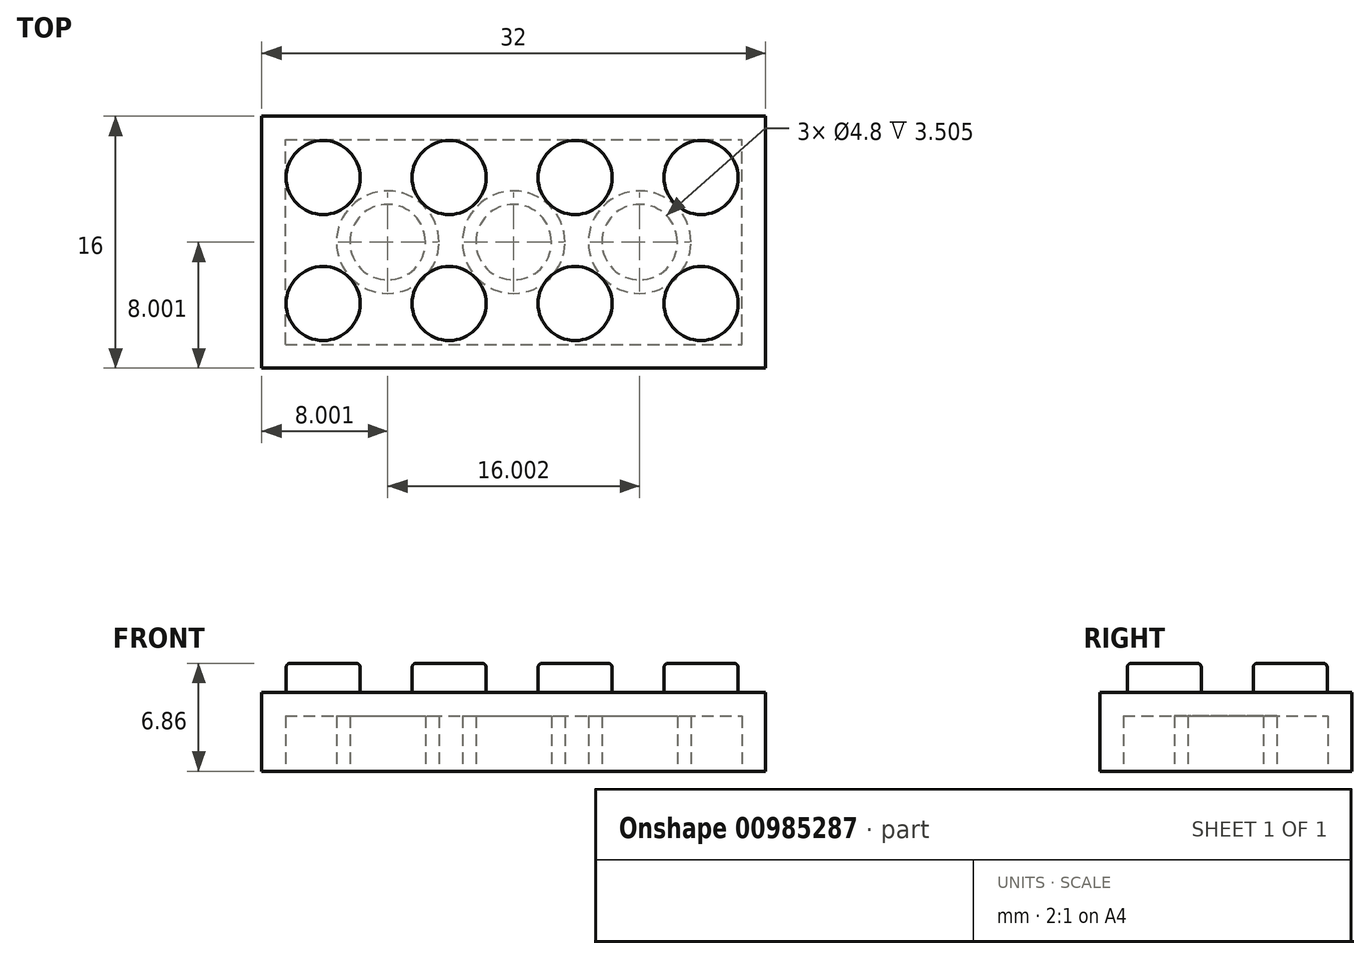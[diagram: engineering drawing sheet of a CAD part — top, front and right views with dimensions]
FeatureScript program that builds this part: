
annotation { "Feature Type Name" : "Feature", "Feature Type Description" : "" }
export const myFeature = defineFeature(function(context is Context, id is Id, definition is map)
    precondition{}
    {
        {
            var Q0;
            Q0=qCreatedBy(makeId("Top.planeOp"),FACE);
            var sketch = newSketch(context, id + "F0", { "sketchPlane" : qUnion([Q0])});
            skLineSegment(sketch, "E0.bottom", {"start": v(0, 0) * mm, "end": v(32, 0) * mm});
            skLineSegment(sketch, "E0.top", {"start": v(0, 16) * mm, "end": v(32, 16) * mm});
            skLineSegment(sketch, "E0.left", {"start": v(0, 0) * mm, "end": v(0, 16) * mm});
            skLineSegment(sketch, "E0.right", {"start": v(32, 0) * mm, "end": v(32, 16) * mm});
            skSolve(sketch);
        }
        {
            var Q0;
            Q0=makeQuery(id+"F0.imprint","IMPRINT",FACE,{"disambiguationData":[TD([[makeQuery(id+"F0.imprint","IMPRINT",EDGE,{"derivedFrom":sQuery(id+"F0.wireOp",EDGE,"E0.bottom")}),1.0]])]});
            extrude(context, id + "F1", {"entities" : qUnion([Q0]), "depth" : 5 * mm, "offsetDistance" : 25.4 * mm});
        }
        {
            var Q0;
            Q0=makeQuery(id+"F1.opExtrude","CAP_FACE",FACE,{"disambiguationData":[OSD([sQuery(id+"F0.wireOp",EDGE,"E0.bottom"),sQuery(id+"F0.wireOp",EDGE,"E0.top"),sQuery(id+"F0.wireOp",EDGE,"E0.left"),sQuery(id+"F0.wireOp",EDGE,"E0.right")])],"isStart":false});
            var sketch = newSketch(context, id + "F2", { "sketchPlane" : qUnion([Q0])});
            skCircle(sketch, "E1", {"center": v(3.9, 12.1) * mm, "radius": 2.35 * mm});
            skCircle(sketch, "E2.0.1.0", {"center": v(3.9, 4.1) * mm, "radius": 2.35 * mm});
            skCircle(sketch, "E2.1.0.0", {"center": v(11.9, 12.1) * mm, "radius": 2.35 * mm});
            skCircle(sketch, "E2.1.1.0", {"center": v(11.9, 4.1) * mm, "radius": 2.35 * mm});
            skCircle(sketch, "E2.2.0.0", {"center": v(19.9, 12.1) * mm, "radius": 2.35 * mm});
            skCircle(sketch, "E2.2.1.0", {"center": v(19.9, 4.1) * mm, "radius": 2.35 * mm});
            skCircle(sketch, "E2.3.0.0", {"center": v(27.9, 12.1) * mm, "radius": 2.35 * mm});
            skCircle(sketch, "E2.3.1.0", {"center": v(27.9, 4.1) * mm, "radius": 2.35 * mm});
            skLineSegment(sketch, "E2.direction1", {"start": v(3.9, 12.1) * mm, "end": v(11.9, 12.1) * mm, "construction": true});
            skLineSegment(sketch, "E2.direction2", {"start": v(3.9, 12.1) * mm, "end": v(3.9, 4.1) * mm, "construction": true});
            skSolve(sketch);
        }
        {
            var Q0;
            Q0 = qSketchRegion(id + "F2", true);
            extrude(context, id + "F3", {"entities" : qUnion([Q0]), "operationType" : NewBodyOperationType.ADD, "depth" : 1.85 * mm, "offsetDistance" : 25.4 * mm});
        }
        {
            var Q0;
            Q0=makeQuery(id+"F3.opExtrude","CAP_EDGE",EDGE,{"disambiguationData":[OSD([sQuery(id+"F2.wireOp",EDGE,"E1")])],"isStart":false});
            var Q1;
            Q1=makeQuery(id+"F3.opExtrude","CAP_FACE",FACE,{"disambiguationData":[OSD([sQuery(id+"F2.wireOp",EDGE,"E2.1.0.0")])],"isStart":false});
            var Q2;
            Q2=makeQuery(id+"F3.opExtrude","CAP_FACE",FACE,{"disambiguationData":[OSD([sQuery(id+"F2.wireOp",EDGE,"E2.2.0.0")])],"isStart":false});
            var Q3;
            Q3=makeQuery(id+"F3.opExtrude","CAP_FACE",FACE,{"disambiguationData":[OSD([sQuery(id+"F2.wireOp",EDGE,"E2.3.0.0")])],"isStart":false});
            var Q4;
            Q4=makeQuery(id+"F3.opExtrude","CAP_FACE",FACE,{"disambiguationData":[OSD([sQuery(id+"F2.wireOp",EDGE,"E2.3.1.0")])],"isStart":false});
            var Q5;
            Q5=makeQuery(id+"F3.opExtrude","CAP_FACE",FACE,{"disambiguationData":[OSD([sQuery(id+"F2.wireOp",EDGE,"E2.2.1.0")])],"isStart":false});
            var Q6;
            Q6=makeQuery(id+"F3.opExtrude","CAP_FACE",FACE,{"disambiguationData":[OSD([sQuery(id+"F2.wireOp",EDGE,"E2.1.1.0")])],"isStart":false});
            var Q7;
            Q7=makeQuery(id+"F3.opExtrude","CAP_FACE",FACE,{"disambiguationData":[OSD([sQuery(id+"F2.wireOp",EDGE,"E2.0.1.0")])],"isStart":false});
            fillet(context, id + "F4", {"entities" : qUnion([Q0, Q1, Q2, Q3, Q4, Q5, Q6, Q7]), "radius" : 0.25 * mm, "tangentPropagation" : true, "allowEdgeOverflow" : false});
        }
        {
            var Q0;
            Q0=makeQuery(id+"F1.opExtrude","CAP_FACE",FACE,{"disambiguationData":[OSD([sQuery(id+"F0.wireOp",EDGE,"E0.bottom"),sQuery(id+"F0.wireOp",EDGE,"E0.top"),sQuery(id+"F0.wireOp",EDGE,"E0.left"),sQuery(id+"F0.wireOp",EDGE,"E0.right")])],"isStart":true});
            var sketch = newSketch(context, id + "F5", { "sketchPlane" : qUnion([Q0])});
            skLineSegment(sketch, "E3.0", {"start": v(1.5, -1.5) * mm, "end": v(30.5, -1.5) * mm});
            skLineSegment(sketch, "E3.1", {"start": v(1.5, -1.5) * mm, "end": v(1.5, -14.5) * mm});
            skLineSegment(sketch, "E3.2", {"start": v(1.5, -14.5) * mm, "end": v(30.5, -14.5) * mm});
            skLineSegment(sketch, "E3.3", {"start": v(30.5, -1.5) * mm, "end": v(30.5, -14.5) * mm});
            skLineSegment(sketch, "E4", {"start": v(0, 0) * mm, "end": v(32, -16) * mm, "construction": true});
            skLineSegment(sketch, "E5", {"start": v(32, -16) * mm, "end": v(0, -16) * mm});
            skLineSegment(sketch, "E6", {"start": v(0, -16) * mm, "end": v(32, 0) * mm, "construction": true});
            skCircle(sketch, "E7", {"center": v(16, -8) * mm, "radius": 2.4 * mm});
            skCircle(sketch, "E8", {"center": v(16, -8) * mm, "radius": 3.25 * mm});
            skCircle(sketch, "E9", {"center": v(8, -8) * mm, "radius": 3.25 * mm});
            skCircle(sketch, "E10", {"center": v(8, -8) * mm, "radius": 2.4 * mm});
            skCircle(sketch, "E11", {"center": v(24, -8) * mm, "radius": 3.25 * mm});
            skCircle(sketch, "E12", {"center": v(24, -8) * mm, "radius": 2.4 * mm});
            skSolve(sketch);
        }
        {
            var Q0;
            Q0 = qSketchRegion(id + "F5", true);
            var Q1;
            Q1=makeQuery(id+"F5.imprint","IMPRINT",FACE,{"disambiguationData":[TD([[makeQuery(id+"F5.imprint","IMPRINT",EDGE,{"derivedFrom":sQuery(id+"F5.wireOp",EDGE,"E10")}),1.0]])]});
            var Q2;
            Q2=makeQuery(id+"F5.imprint","IMPRINT",FACE,{"disambiguationData":[TD([[makeQuery(id+"F5.imprint","IMPRINT",EDGE,{"derivedFrom":sQuery(id+"F5.wireOp",EDGE,"E7")}),1.0]])]});
            var Q3;
            Q3=makeQuery(id+"F5.imprint","IMPRINT",FACE,{"disambiguationData":[TD([[makeQuery(id+"F5.imprint","IMPRINT",EDGE,{"derivedFrom":sQuery(id+"F5.wireOp",EDGE,"E12")}),1.0]])]});
            extrude(context, id + "F6", {"entities" : qUnion([Q0, Q1, Q2, Q3]), "operationType" : NewBodyOperationType.REMOVE, "oppositeDirection" : true, "depth" : 3.5 * mm, "offsetDistance" : 25.4 * mm});
        }
    });
